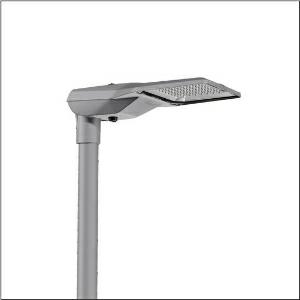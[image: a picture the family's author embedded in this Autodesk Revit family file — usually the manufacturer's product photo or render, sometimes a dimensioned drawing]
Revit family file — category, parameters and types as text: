
# Revit family: streetlight_sl_21_midi___pl52_5xe3h33t08lb_7b8b
name_source: partatom
category: Lighting Fixtures
units: mm (PartAtom-declared; Revit-internal decimal feet)

## family parameters
Cut with Voids When Loaded = No
Host = Face
Light Source = No
Part Type = Normal
Room Calculation Point = No
Round Connector Dimension = Use Diameter
Shared = No

## types (1)
- --- (1 x LED, 14100 lm, 99.6 W, 3000K)
    Apparent Load = 100 VA
    CIE Flux Codes = 27 59 98 100 100
    Color Rendering = 70
    Color Temperature = 3000K
    Default Elevation = 1800 mm
    Description = Streetlight SL 21 midi, mast luminaire, primary light control with lens, of PMMA, primary optical cover: cover, of toughened safety glass, transparent, light distribution: PL52, light emission: direct distribution, primary light characteristic: asymmetric, installation type: side-entry, post-top, LED, High Power LED, rated luminous flux: 14.100lm, luminous efficacy: 142lm/W, light colour: 730, colour temperature: 3000K, control gear: D4i, control: overheat protection, constant luminous flux control, time-dependent luminous flux control, flexible luminous flux parameterisation, pre-setting: logarithmic dimming characteristic, mains connection: 230..240V, AC, 50/60Hz, start of lifetime: 100W, end of service life: 102W, reduction: 46W, luminaire housing, of diecast aluminium, powder-coated, Siteco® metallic grey (DB 702S), corrosivity category C5 mid according to DIN EN ISO 12944, please order mast flange separately, inclination adjustable: 0°, 5°, 10°, 15°, sealing non-destructively replaceable, multi-level sealing system, length: 644mm, width: 335mm, height: 110mm, mast flange for spigot size: 42mm (side-entry): 5XC10008XM4, 60/48mm (side-entry/post-top): 5XC10108XM2, 76/60mm (side-entry/post-top): 5XC10108XM1, mounting height: 4..8m, Smart Interface below and above, protection rating (complete): IP66, insulation class (complete): insulation class II (safety insulation), certification: CE, ENEC, ENEC+, VDE, impact resistance: IK10, permissible operating ambient temperature for outdoor applications: -40..+50°C, standard-compliant lighting for roads and squares, packaging unit: 1 piece

Light Distribution: PL52
    Height = 111 mm
    Lamp = 1 x LED
    Lamp Light Flux = 14100 lm
    Lamp Power = 99.6 W
    Lamp count = 1
    Length = 644 mm
    Luminous efficacy = 142 lm/W
    Manufacturer = Siteco
    ModVariant = No
    Model = 5XE3H33T08LB
    Number of Poles = 1
    OnlyDefault = Yes
    Power Factor = 1
    Product Name = Streetlight SL 21 midi | PL52
    Product group = mast luminaire | pylon top
    ProductGroupID = 6100
    Protection Class = Protection class II
    Protection Degree = IP 66
    RLX_Detail_Level = 1
    RLX_Emergency_Light_Flux = 0 lm
    RLX_Emergency_Type = 0
    RLX_Emergency_Type_DB = No
    RlxData = <blob elided: 36549 chars, md5=bbca55fc>
    Socket = socket
    Standby Power = 0 W
    System Light Flux = 14100 lm
    System Power = 100 W
    Type Comments = factory setting: luminous flux: 100 % | dim-lin: 254 | 1020 mA
    Type Image = l_1004304.jpg
    URL = http://relux.com
    VarID = @adj_032389
    Voltage = 0 V
    Weight = 0.00 kg
    Width = 336 mm

## geometry (parser evidence)
native form markers: Blend x4, Sweep x11
no freeform markers — native parametric forms only
